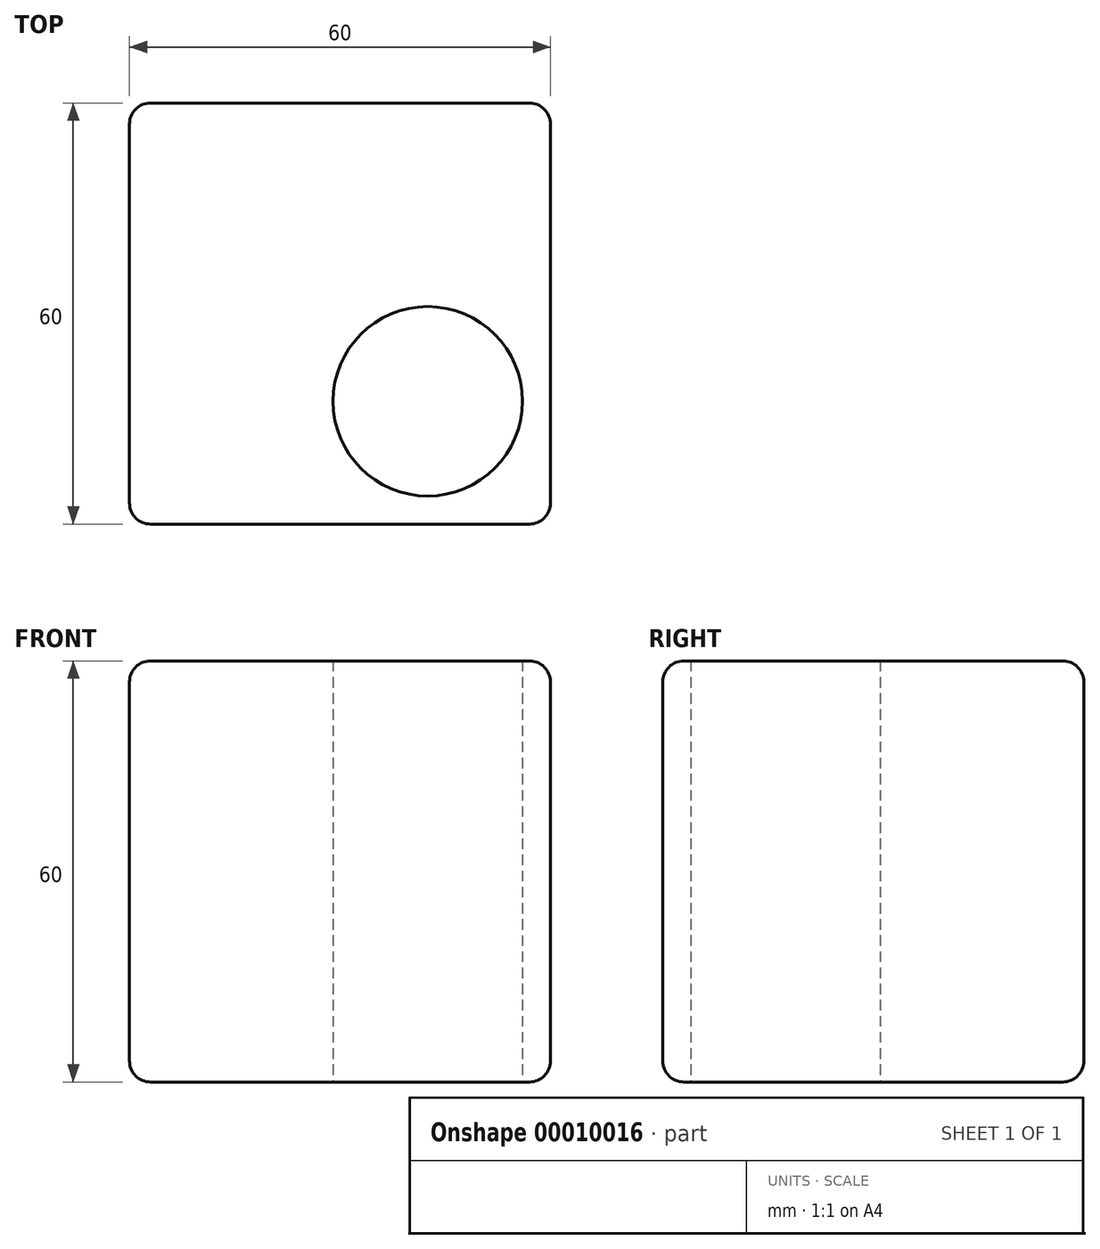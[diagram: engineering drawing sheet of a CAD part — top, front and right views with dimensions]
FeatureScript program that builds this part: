
annotation { "Feature Type Name" : "Feature", "Feature Type Description" : "" }
export const myFeature = defineFeature(function(context is Context, id is Id, definition is map)
    precondition{}
    {
        {
            var Q0;
            Q0=qCreatedBy(makeId("Top.planeOp"),FACE);
            var sketch = newSketch(context, id + "F0", { "sketchPlane" : qUnion([Q0])});
            skLineSegment(sketch, "E0.bottom", {"start": v(-30, 30) * mm, "end": v(30, 30) * mm});
            skLineSegment(sketch, "E0.top", {"start": v(-30, -30) * mm, "end": v(30, -30) * mm});
            skLineSegment(sketch, "E0.left", {"start": v(-30, 30) * mm, "end": v(-30, -30) * mm});
            skLineSegment(sketch, "E0.right", {"start": v(30, 30) * mm, "end": v(30, -30) * mm});
            skCircle(sketch, "E1", {"center": v(12.5, -12.5) * mm, "radius": 13.5 * mm});
            skSolve(sketch);
        }
        {
            var Q0;
            Q0 = qSketchRegion(id + "F0", true);
            extrude(context, id + "F1", {"entities" : qUnion([Q0]), "depth" : 60 * mm});
        }
        {
            var Q0;
            Q0=makeQuery(id+"F1.opExtrude","CAP_EDGE",EDGE,{"disambiguationData":[OSD([sQuery(id+"F0.wireOp",EDGE,"E0.bottom")])],"isStart":false});
            var Q1;
            Q1=makeQuery(id+"F1.opExtrude","CAP_EDGE",EDGE,{"disambiguationData":[OSD([sQuery(id+"F0.wireOp",EDGE,"E0.right")])],"isStart":false});
            var Q2;
            Q2=makeQuery(id+"F1.opExtrude","CAP_EDGE",EDGE,{"disambiguationData":[OSD([sQuery(id+"F0.wireOp",EDGE,"E0.left")])],"isStart":true});
            var Q3;
            Q3=makeQuery(id+"F1.opExtrude","CAP_EDGE",EDGE,{"disambiguationData":[OSD([sQuery(id+"F0.wireOp",EDGE,"E0.top")])],"isStart":false});
            var Q4;
            Q4=makeQuery(id+"F1.opExtrude","CAP_EDGE",EDGE,{"disambiguationData":[OSD([sQuery(id+"F0.wireOp",EDGE,"E0.left")])],"isStart":false});
            var Q5;
            Q5=makeQuery(id+"F1.opExtrude","SWEPT_EDGE",EDGE,{"disambiguationData":[OSD([sQuery(id+"F0.wireOp",EDGE,"E0.top"),sQuery(id+"F0.wireOp",EDGE,"E0.left")])]});
            var Q6;
            Q6=makeQuery(id+"F1.opExtrude","SWEPT_EDGE",EDGE,{"disambiguationData":[OSD([sQuery(id+"F0.wireOp",EDGE,"E0.top"),sQuery(id+"F0.wireOp",EDGE,"E0.right")])]});
            var Q7;
            Q7=makeQuery(id+"F1.opExtrude","CAP_EDGE",EDGE,{"disambiguationData":[OSD([sQuery(id+"F0.wireOp",EDGE,"E0.top")])],"isStart":true});
            var Q8;
            Q8=makeQuery(id+"F1.opExtrude","CAP_EDGE",EDGE,{"disambiguationData":[OSD([sQuery(id+"F0.wireOp",EDGE,"E0.right")])],"isStart":true});
            var Q9;
            Q9=makeQuery(id+"F1.opExtrude","SWEPT_EDGE",EDGE,{"disambiguationData":[OSD([sQuery(id+"F0.wireOp",EDGE,"E0.bottom"),sQuery(id+"F0.wireOp",EDGE,"E0.right")])]});
            var Q10;
            Q10=makeQuery(id+"F1.opExtrude","CAP_EDGE",EDGE,{"disambiguationData":[OSD([sQuery(id+"F0.wireOp",EDGE,"E0.bottom")])],"isStart":true});
            var Q11;
            Q11=makeQuery(id+"F1.opExtrude","SWEPT_EDGE",EDGE,{"disambiguationData":[OSD([sQuery(id+"F0.wireOp",EDGE,"E0.bottom"),sQuery(id+"F0.wireOp",EDGE,"E0.left")])]});
            fillet(context, id + "F2", {"entities" : qUnion([Q0, Q1, Q2, Q3, Q4, Q5, Q6, Q7, Q8, Q9, Q10, Q11]), "radius" : 3 * mm, "tangentPropagation" : true, "allowEdgeOverflow" : false});
        }
    });
